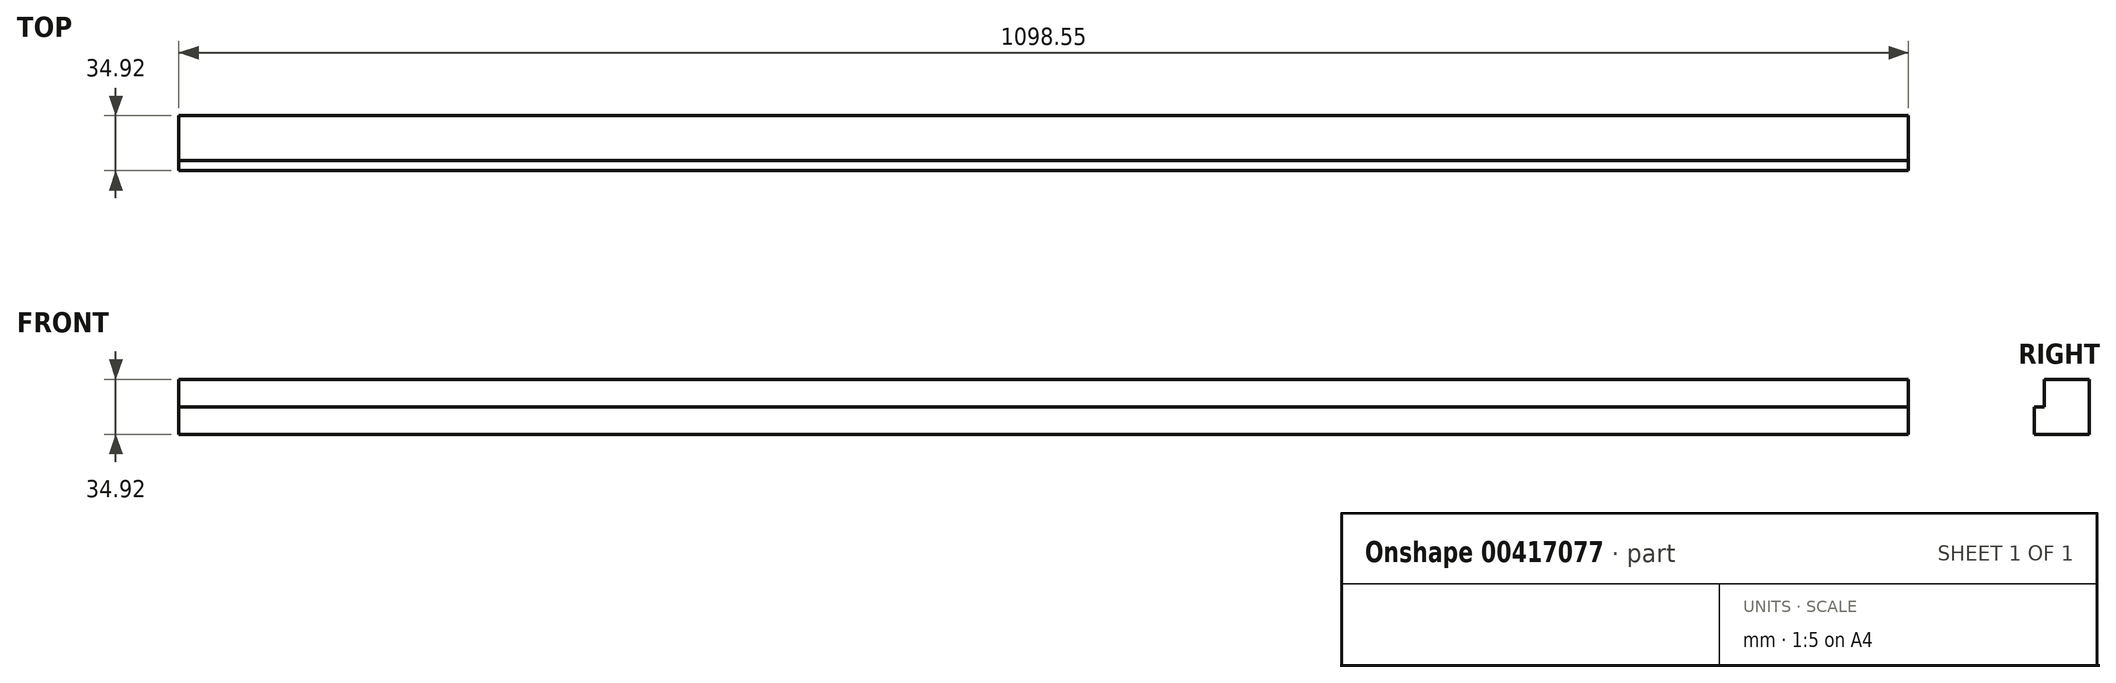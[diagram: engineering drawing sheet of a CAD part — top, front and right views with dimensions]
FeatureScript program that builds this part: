
annotation { "Feature Type Name" : "Feature", "Feature Type Description" : "" }
export const myFeature = defineFeature(function(context is Context, id is Id, definition is map)
    precondition{}
    {
        {
            var Q0;
            Q0=qCreatedBy(makeId("Right.planeOp"),FACE);
            var sketch = newSketch(context, id + "F0", { "sketchPlane" : qUnion([Q0])});
            skLineSegment(sketch, "E0.bottom", {"start": v(17.46, 17.46) * mm, "end": v(-17.46, 17.46) * mm});
            skLineSegment(sketch, "E0.top", {"start": v(17.46, -17.46) * mm, "end": v(-17.46, -17.46) * mm});
            skLineSegment(sketch, "E0.left", {"start": v(17.46, 17.46) * mm, "end": v(17.46, -17.46) * mm});
            skLineSegment(sketch, "E0.right", {"start": v(-17.46, 17.46) * mm, "end": v(-17.46, -17.46) * mm});
            skPoint(sketch, "E0.middle", {"position": v(0, 0) * mm});
            skSolve(sketch);
        }
        {
            var Q0;
            Q0 = qSketchRegion(id + "F0", true);
            extrude(context, id + "F1", {"entities" : qUnion([Q0]), "depth" : 1098.55 * mm});
        }
        {
            var Q0;
            Q0=makeQuery(id+"F1.opExtrude","CAP_FACE",FACE,{"disambiguationData":[OSD([sQuery(id+"F0.wireOp",EDGE,"E0.bottom"),sQuery(id+"F0.wireOp",EDGE,"E0.top"),sQuery(id+"F0.wireOp",EDGE,"E0.left"),sQuery(id+"F0.wireOp",EDGE,"E0.right")])],"isStart":false});
            var sketch = newSketch(context, id + "F2", { "sketchPlane" : qUnion([Q0])});
            skLineSegment(sketch, "E1.bottom", {"start": v(-17.46, 17.46) * mm, "end": v(-11.11, 17.46) * mm});
            skLineSegment(sketch, "E1.top", {"start": v(-17.46, 0) * mm, "end": v(-11.11, 0) * mm});
            skLineSegment(sketch, "E1.left", {"start": v(-17.46, 17.46) * mm, "end": v(-17.46, 0) * mm});
            skLineSegment(sketch, "E1.right", {"start": v(-11.11, 17.46) * mm, "end": v(-11.11, 0) * mm});
            skSolve(sketch);
        }
        {
            var Q0;
            Q0 = qSketchRegion(id + "F2", true);
            extrude(context, id + "F3", {"entities" : qUnion([Q0]), "operationType" : NewBodyOperationType.REMOVE, "endBound" : BoundingType.THROUGH_ALL, "oppositeDirection" : true, "depth" : 25.4 * mm, "offsetDistance" : 25.4 * mm});
        }
    });
